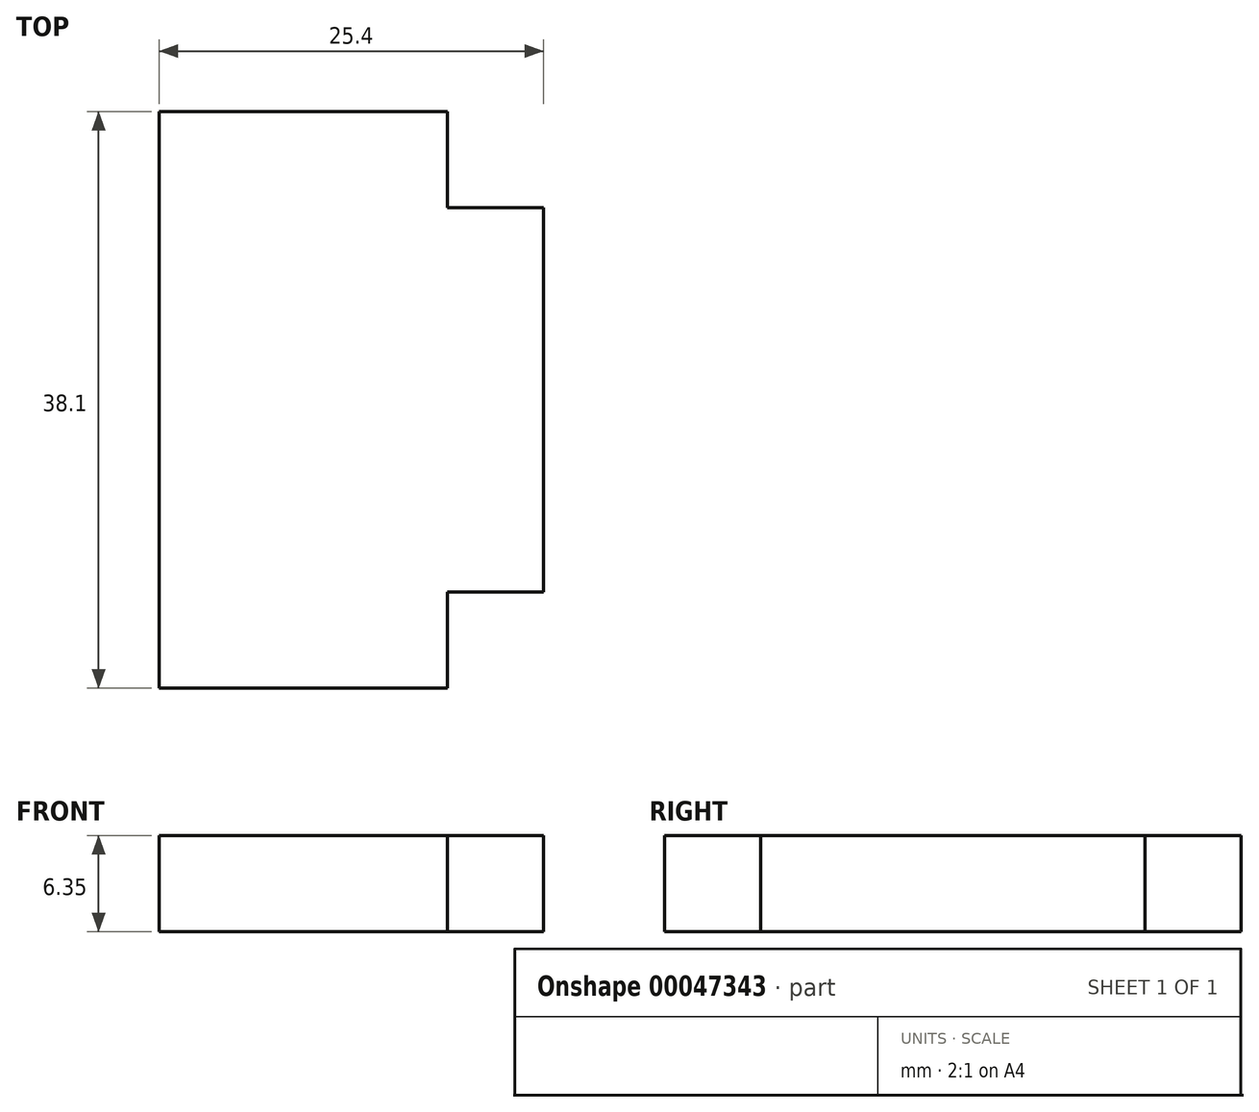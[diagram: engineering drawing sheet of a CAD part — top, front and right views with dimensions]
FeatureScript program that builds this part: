
annotation { "Feature Type Name" : "Feature", "Feature Type Description" : "" }
export const myFeature = defineFeature(function(context is Context, id is Id, definition is map)
    precondition{}
    {
        {
            var Q0;
            Q0=qCreatedBy(makeId("Top.planeOp"),FACE);
            var sketch = newSketch(context, id + "F0", { "sketchPlane" : qUnion([Q0])});
            skLineSegment(sketch, "E0", {"start": v(0, 4.95) * mm, "end": v(0, -33.15) * mm});
            skLineSegment(sketch, "E1", {"start": v(0, -33.15) * mm, "end": v(19.05, -33.15) * mm});
            skLineSegment(sketch, "E2", {"start": v(19.05, -33.15) * mm, "end": v(19.05, -26.8) * mm});
            skLineSegment(sketch, "E3", {"start": v(19.05, -26.8) * mm, "end": v(25.4, -26.8) * mm});
            skLineSegment(sketch, "E4", {"start": v(25.4, -26.8) * mm, "end": v(25.4, -1.4) * mm});
            skLineSegment(sketch, "E5", {"start": v(25.4, -1.4) * mm, "end": v(19.05, -1.4) * mm});
            skLineSegment(sketch, "E6", {"start": v(19.05, -1.4) * mm, "end": v(19.05, 4.95) * mm});
            skLineSegment(sketch, "E7", {"start": v(19.05, 4.95) * mm, "end": v(0, 4.95) * mm});
            skSolve(sketch);
        }
        {
            var Q0;
            Q0 = qSketchRegion(id + "F0", true);
            extrude(context, id + "F1", {"entities" : qUnion([Q0]), "depth" : 6.35 * mm});
        }
    });
